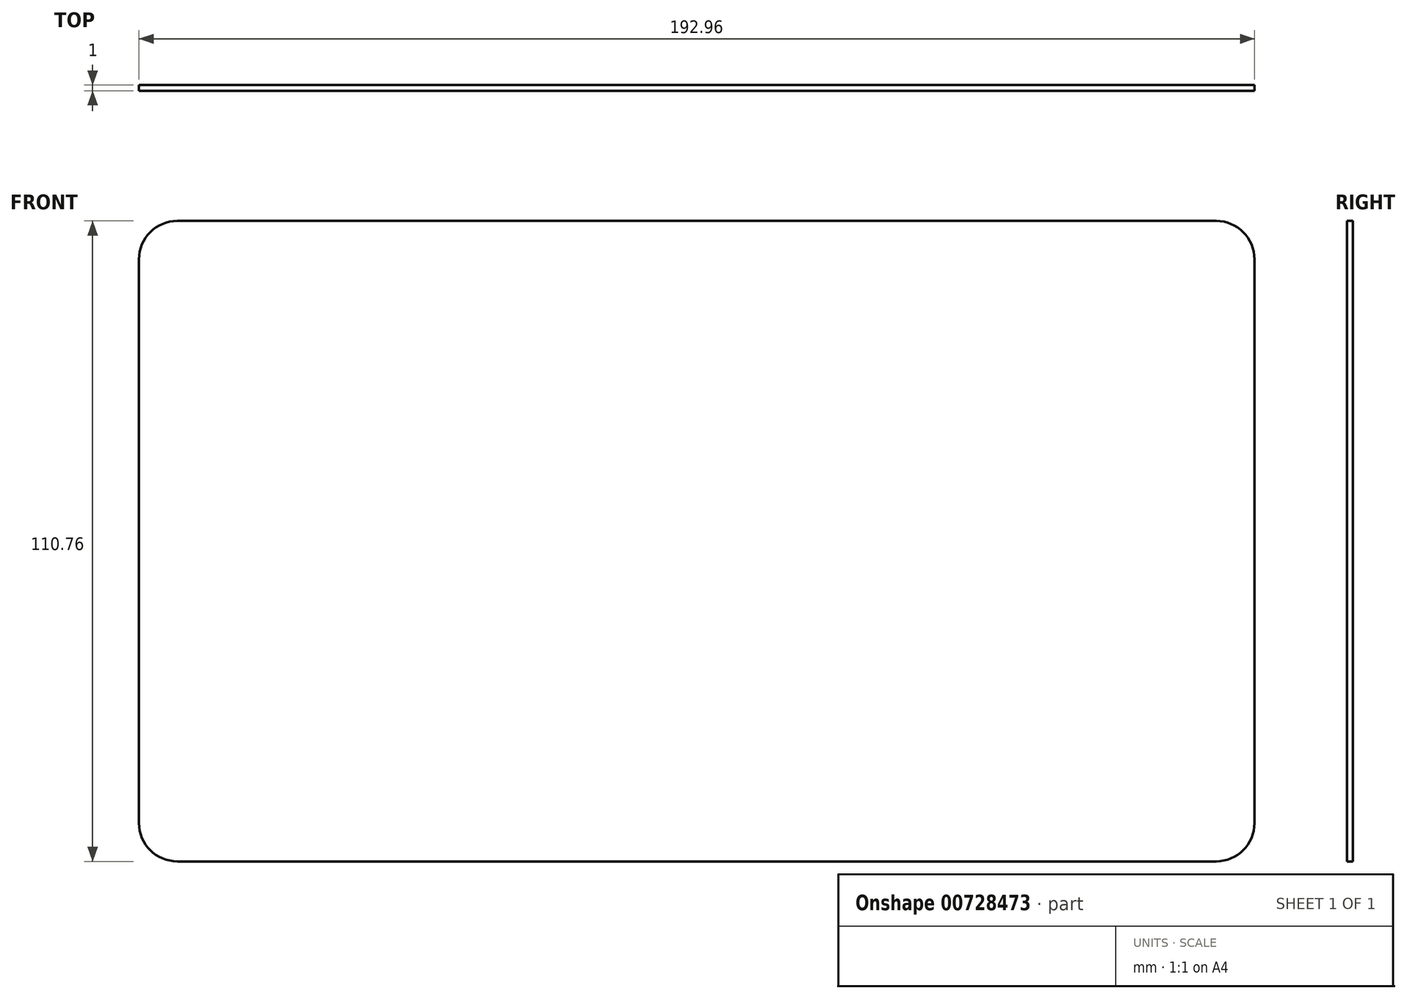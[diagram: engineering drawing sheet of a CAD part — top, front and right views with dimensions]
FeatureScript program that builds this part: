
annotation { "Feature Type Name" : "Feature", "Feature Type Description" : "" }
export const myFeature = defineFeature(function(context is Context, id is Id, definition is map)
    precondition{}
    {
        {
            var Q0;
            Q0=qCreatedBy(makeId("Front.planeOp"),FACE);
            var sketch = newSketch(context, id + "F0", { "sketchPlane" : qUnion([Q0])});
            skLineSegment(sketch, "E0.bottom", {"start": v(-89.85, 55.38) * mm, "end": v(89.85, 55.38) * mm});
            skLineSegment(sketch, "E0.top", {"start": v(-89.85, -55.38) * mm, "end": v(89.85, -55.38) * mm});
            skLineSegment(sketch, "E0.left", {"start": v(-96.48, 48.75) * mm, "end": v(-96.48, -48.75) * mm});
            skLineSegment(sketch, "E0.right", {"start": v(96.48, 48.75) * mm, "end": v(96.48, -48.75) * mm});
            skPoint(sketch, "E0.middle", {"position": v(0, 0) * mm});
            skPoint(sketch, "E1.visualSharp", {"position": v(-96.48, 55.38) * mm});
            skArc(sketch, "E1.filletArc", {"start": v(-89.85, 55.38) * mm, "mid": v(-94.54, 53.44) * mm, "end": v(-96.48, 48.75) * mm});
            skPoint(sketch, "E2.visualSharp", {"position": v(96.48, 55.38) * mm});
            skArc(sketch, "E2.filletArc", {"start": v(96.48, 48.75) * mm, "mid": v(94.54, 53.44) * mm, "end": v(89.85, 55.38) * mm});
            skPoint(sketch, "E3.visualSharp", {"position": v(96.48, -55.38) * mm});
            skArc(sketch, "E3.filletArc", {"start": v(89.85, -55.38) * mm, "mid": v(94.54, -53.44) * mm, "end": v(96.48, -48.75) * mm});
            skPoint(sketch, "E4.visualSharp", {"position": v(-96.48, -55.38) * mm});
            skArc(sketch, "E4.filletArc", {"start": v(-96.48, -48.75) * mm, "mid": v(-94.54, -53.44) * mm, "end": v(-89.85, -55.38) * mm});
            skLineSegment(sketch, "E5.bottom", {"start": v(-84.5, 48.75) * mm, "end": v(81.7, 48.75) * mm});
            skLineSegment(sketch, "E5.top", {"start": v(-84.5, -51.31) * mm, "end": v(81.7, -51.31) * mm});
            skLineSegment(sketch, "E5.left", {"start": v(-84.5, 48.75) * mm, "end": v(-84.5, -51.3) * mm});
            skLineSegment(sketch, "E5.right", {"start": v(81.7, 48.75) * mm, "end": v(81.7, -51.3) * mm});
            skPoint(sketch, "E5.middle", {"position": v(-1.4, -1.28) * mm});
            skLineSegment(sketch, "E6.bottom", {"start": v(-57.5, 29.8) * mm, "end": v(-71.5, 29.8) * mm});
            skLineSegment(sketch, "E6.top", {"start": v(-57.5, 37.8) * mm, "end": v(-71.5, 37.8) * mm});
            skLineSegment(sketch, "E6.left", {"start": v(-57.5, 29.8) * mm, "end": v(-57.5, 37.8) * mm});
            skLineSegment(sketch, "E6.right", {"start": v(-71.5, 29.8) * mm, "end": v(-71.5, 37.8) * mm});
            skPoint(sketch, "E6.middle", {"position": v(-64.5, 33.8) * mm});
            skLineSegment(sketch, "E7.bottom", {"start": v(68.7, 29.8) * mm, "end": v(54.7, 29.8) * mm});
            skLineSegment(sketch, "E7.top", {"start": v(68.7, 37.8) * mm, "end": v(54.7, 37.8) * mm});
            skLineSegment(sketch, "E7.left", {"start": v(68.7, 29.8) * mm, "end": v(68.7, 37.8) * mm});
            skLineSegment(sketch, "E7.right", {"start": v(54.7, 29.8) * mm, "end": v(54.7, 37.8) * mm});
            skPoint(sketch, "E7.middle", {"position": v(61.7, 33.8) * mm});
            skLineSegment(sketch, "E8.bottom", {"start": v(-57.5, -35.85) * mm, "end": v(-71.5, -35.85) * mm});
            skLineSegment(sketch, "E8.top", {"start": v(-57.5, -27.85) * mm, "end": v(-71.5, -27.85) * mm});
            skLineSegment(sketch, "E8.left", {"start": v(-57.5, -35.85) * mm, "end": v(-57.5, -27.85) * mm});
            skLineSegment(sketch, "E8.right", {"start": v(-71.5, -35.85) * mm, "end": v(-71.5, -27.85) * mm});
            skPoint(sketch, "E8.middle", {"position": v(-64.5, -31.85) * mm});
            skLineSegment(sketch, "E9.bottom", {"start": v(68.7, -35.85) * mm, "end": v(54.7, -35.85) * mm});
            skLineSegment(sketch, "E9.top", {"start": v(68.7, -27.85) * mm, "end": v(54.7, -27.85) * mm});
            skLineSegment(sketch, "E9.left", {"start": v(68.7, -35.85) * mm, "end": v(68.7, -27.85) * mm});
            skLineSegment(sketch, "E9.right", {"start": v(54.7, -35.85) * mm, "end": v(54.7, -27.85) * mm});
            skPoint(sketch, "E9.middle", {"position": v(61.7, -31.85) * mm});
            skCircle(sketch, "E10", {"center": v(-64.5, 33.8) * mm, "radius": 1.5 * mm});
            skCircle(sketch, "E11", {"center": v(61.7, 33.8) * mm, "radius": 1.5 * mm});
            skCircle(sketch, "E12", {"center": v(61.7, -31.85) * mm, "radius": 1.5 * mm});
            skCircle(sketch, "E13", {"center": v(-64.5, -31.85) * mm, "radius": 1.5 * mm});
            skLineSegment(sketch, "E14.bottom", {"start": v(-40.05, 20.95) * mm, "end": v(-32.05, 20.95) * mm});
            skLineSegment(sketch, "E14.top", {"start": v(-40.05, 34.95) * mm, "end": v(-32.05, 34.95) * mm});
            skLineSegment(sketch, "E14.left", {"start": v(-40.05, 20.95) * mm, "end": v(-40.05, 34.95) * mm});
            skLineSegment(sketch, "E14.right", {"start": v(-32.05, 20.95) * mm, "end": v(-32.05, 34.95) * mm});
            skPoint(sketch, "E14.middle", {"position": v(-36.05, 27.95) * mm});
            skLineSegment(sketch, "E15.bottom", {"start": v(-40.05, -14.05) * mm, "end": v(-32.05, -14.05) * mm});
            skLineSegment(sketch, "E15.top", {"start": v(-40.05, -28.05) * mm, "end": v(-32.05, -28.05) * mm});
            skLineSegment(sketch, "E15.left", {"start": v(-40.05, -14.05) * mm, "end": v(-40.05, -28.05) * mm});
            skLineSegment(sketch, "E15.right", {"start": v(-32.05, -14.05) * mm, "end": v(-32.05, -28.05) * mm});
            skPoint(sketch, "E15.middle", {"position": v(-36.05, -21.05) * mm});
            skLineSegment(sketch, "E16.bottom", {"start": v(17.95, -14.05) * mm, "end": v(25.95, -14.05) * mm});
            skLineSegment(sketch, "E16.top", {"start": v(17.95, -28.05) * mm, "end": v(25.95, -28.05) * mm});
            skLineSegment(sketch, "E16.left", {"start": v(17.95, -14.05) * mm, "end": v(17.95, -28.05) * mm});
            skLineSegment(sketch, "E16.right", {"start": v(25.95, -14.05) * mm, "end": v(25.95, -28.05) * mm});
            skPoint(sketch, "E16.middle", {"position": v(21.95, -21.05) * mm});
            skLineSegment(sketch, "E17.bottom", {"start": v(17.95, 20.95) * mm, "end": v(25.95, 20.95) * mm});
            skLineSegment(sketch, "E17.top", {"start": v(17.95, 34.95) * mm, "end": v(25.95, 34.95) * mm});
            skLineSegment(sketch, "E17.left", {"start": v(17.95, 20.95) * mm, "end": v(17.95, 34.95) * mm});
            skLineSegment(sketch, "E17.right", {"start": v(25.95, 20.95) * mm, "end": v(25.95, 34.95) * mm});
            skPoint(sketch, "E17.middle", {"position": v(21.95, 27.95) * mm});
            skCircle(sketch, "E18", {"center": v(-36.05, 27.95) * mm, "radius": 1.25 * mm});
            skCircle(sketch, "E19", {"center": v(21.95, 27.95) * mm, "radius": 1.25 * mm});
            skCircle(sketch, "E20", {"center": v(21.95, -21.05) * mm, "radius": 1.25 * mm});
            skCircle(sketch, "E21", {"center": v(-36.05, -21.05) * mm, "radius": 1.25 * mm});
            skLineSegment(sketch, "E22.bottom", {"start": v(-40.05, 24.95) * mm, "end": v(-32.05, 24.95) * mm});
            skLineSegment(sketch, "E22.top", {"start": v(-40.05, 30.95) * mm, "end": v(-32.05, 30.95) * mm});
            skLineSegment(sketch, "E22.left", {"start": v(-40.05, 24.95) * mm, "end": v(-40.05, 30.95) * mm});
            skLineSegment(sketch, "E22.right", {"start": v(-32.05, 24.95) * mm, "end": v(-32.05, 30.95) * mm});
            skLineSegment(sketch, "E23.bottom", {"start": v(17.95, 24.95) * mm, "end": v(25.95, 24.95) * mm});
            skLineSegment(sketch, "E23.top", {"start": v(17.95, 30.95) * mm, "end": v(25.95, 30.95) * mm});
            skLineSegment(sketch, "E23.left", {"start": v(17.95, 24.95) * mm, "end": v(17.95, 30.95) * mm});
            skLineSegment(sketch, "E23.right", {"start": v(25.95, 24.95) * mm, "end": v(25.95, 30.95) * mm});
            skLineSegment(sketch, "E24.bottom", {"start": v(17.95, -18.05) * mm, "end": v(25.95, -18.05) * mm});
            skLineSegment(sketch, "E24.top", {"start": v(17.95, -24.05) * mm, "end": v(25.95, -24.05) * mm});
            skLineSegment(sketch, "E24.left", {"start": v(17.95, -18.05) * mm, "end": v(17.95, -24.05) * mm});
            skLineSegment(sketch, "E24.right", {"start": v(25.95, -18.05) * mm, "end": v(25.95, -24.05) * mm});
            skLineSegment(sketch, "E25.bottom", {"start": v(-40.05, -18.05) * mm, "end": v(-32.05, -18.05) * mm});
            skLineSegment(sketch, "E25.top", {"start": v(-40.05, -24.05) * mm, "end": v(-32.05, -24.05) * mm});
            skLineSegment(sketch, "E25.left", {"start": v(-40.05, -18.05) * mm, "end": v(-40.05, -24.05) * mm});
            skLineSegment(sketch, "E25.right", {"start": v(-32.05, -18.05) * mm, "end": v(-32.05, -24.05) * mm});
            skLineSegment(sketch, "E26.bottom", {"start": v(-67.5, 37.8) * mm, "end": v(-61.5, 37.8) * mm});
            skLineSegment(sketch, "E26.top", {"start": v(-67.5, 29.8) * mm, "end": v(-61.5, 29.8) * mm});
            skLineSegment(sketch, "E26.left", {"start": v(-67.5, 37.8) * mm, "end": v(-67.5, 29.8) * mm});
            skLineSegment(sketch, "E26.right", {"start": v(-61.5, 37.8) * mm, "end": v(-61.5, 29.8) * mm});
            skLineSegment(sketch, "E27.bottom", {"start": v(-67.5, -27.85) * mm, "end": v(-61.5, -27.85) * mm});
            skLineSegment(sketch, "E27.top", {"start": v(-67.5, -35.85) * mm, "end": v(-61.5, -35.85) * mm});
            skLineSegment(sketch, "E27.left", {"start": v(-67.5, -27.85) * mm, "end": v(-67.5, -35.85) * mm});
            skLineSegment(sketch, "E27.right", {"start": v(-61.5, -27.85) * mm, "end": v(-61.5, -35.85) * mm});
            skLineSegment(sketch, "E28.bottom", {"start": v(58.7, -27.85) * mm, "end": v(64.7, -27.85) * mm});
            skLineSegment(sketch, "E28.top", {"start": v(58.7, -35.85) * mm, "end": v(64.7, -35.85) * mm});
            skLineSegment(sketch, "E28.left", {"start": v(58.7, -27.85) * mm, "end": v(58.7, -35.85) * mm});
            skLineSegment(sketch, "E28.right", {"start": v(64.7, -27.85) * mm, "end": v(64.7, -35.85) * mm});
            skLineSegment(sketch, "E29.bottom", {"start": v(58.7, 37.8) * mm, "end": v(64.7, 37.8) * mm});
            skLineSegment(sketch, "E29.top", {"start": v(58.7, 29.8) * mm, "end": v(64.7, 29.8) * mm});
            skLineSegment(sketch, "E29.left", {"start": v(58.7, 37.8) * mm, "end": v(58.7, 29.8) * mm});
            skLineSegment(sketch, "E29.right", {"start": v(64.7, 37.8) * mm, "end": v(64.7, 29.8) * mm});
            skSolve(sketch);
        }
        {
            var Q0;
            Q0=makeQuery(id+"F0.imprint","IMPRINT",FACE,{"disambiguationData":[TD([[makeQuery(id+"F0.imprint","IMPRINT",EDGE,{"derivedFrom":sQuery(id+"F0.wireOp",EDGE,"E13")}),-1.0]])]});
            var Q1;
            {var subQ0=sQuery(id+"F0.wireOp",EDGE,"E17.top");Q1=makeQuery(id+"F0.imprint","IMPRINT",FACE,{"disambiguationData":[TD([[makeQuery(id+"F0.imprint","IMPRINT",EDGE,{"derivedFrom":subQ0}),-1.0]])]});}
            var Q2;
            Q2=makeQuery(id+"F0.imprint","IMPRINT",FACE,{"disambiguationData":[TD([[makeQuery(id+"F0.imprint","IMPRINT",EDGE,{"derivedFrom":sQuery(id+"F0.wireOp",EDGE,"E5.bottom")}),-1.0]])]});
            var Q3;
            {var subQ0=sQuery(id+"F0.wireOp",EDGE,"E14.bottom");Q3=makeQuery(id+"F0.imprint","IMPRINT",FACE,{"disambiguationData":[TD([[makeQuery(id+"F0.imprint","IMPRINT",EDGE,{"derivedFrom":subQ0}),1.0]])]});}
            var Q4;
            Q4=makeQuery(id+"F0.imprint","IMPRINT",FACE,{"disambiguationData":[TD([[makeQuery(id+"F0.imprint","IMPRINT",EDGE,{"derivedFrom":sQuery(id+"F0.wireOp",EDGE,"E19")}),-1.0]])]});
            var Q5;
            {var subQ0=sQuery(id+"F0.wireOp",EDGE,"E16.bottom");Q5=makeQuery(id+"F0.imprint","IMPRINT",FACE,{"disambiguationData":[TD([[makeQuery(id+"F0.imprint","IMPRINT",EDGE,{"derivedFrom":subQ0}),-1.0]])]});}
            var Q6;
            {var subQ0=sQuery(id+"F0.wireOp",EDGE,"E17.bottom");Q6=makeQuery(id+"F0.imprint","IMPRINT",FACE,{"disambiguationData":[TD([[makeQuery(id+"F0.imprint","IMPRINT",EDGE,{"derivedFrom":subQ0}),1.0]])]});}
            var Q7;
            Q7=makeQuery(id+"F0.imprint","IMPRINT",FACE,{"disambiguationData":[TD([[makeQuery(id+"F0.imprint","IMPRINT",EDGE,{"derivedFrom":sQuery(id+"F0.wireOp",EDGE,"E12")}),-1.0]])]});
            var Q8;
            Q8=makeQuery(id+"F0.imprint","IMPRINT",FACE,{"disambiguationData":[TD([[makeQuery(id+"F0.imprint","IMPRINT",EDGE,{"derivedFrom":sQuery(id+"F0.wireOp",EDGE,"E21")}),-1.0]])]});
            var Q9;
            {var subQ0=sQuery(id+"F0.wireOp",EDGE,"E7.right");Q9=makeQuery(id+"F0.imprint","IMPRINT",FACE,{"disambiguationData":[TD([[makeQuery(id+"F0.imprint","IMPRINT",EDGE,{"derivedFrom":subQ0}),-1.0]])]});}
            var Q10;
            {var subQ0=sQuery(id+"F0.wireOp",EDGE,"E7.left");Q10=makeQuery(id+"F0.imprint","IMPRINT",FACE,{"disambiguationData":[TD([[makeQuery(id+"F0.imprint","IMPRINT",EDGE,{"derivedFrom":subQ0}),1.0]])]});}
            var Q11;
            {var subQ0=sQuery(id+"F0.wireOp",EDGE,"E6.right");Q11=makeQuery(id+"F0.imprint","IMPRINT",FACE,{"disambiguationData":[TD([[makeQuery(id+"F0.imprint","IMPRINT",EDGE,{"derivedFrom":subQ0}),-1.0]])]});}
            var Q12;
            {var subQ0=sQuery(id+"F0.wireOp",EDGE,"E6.left");Q12=makeQuery(id+"F0.imprint","IMPRINT",FACE,{"disambiguationData":[TD([[makeQuery(id+"F0.imprint","IMPRINT",EDGE,{"derivedFrom":subQ0}),1.0]])]});}
            var Q13;
            {var subQ0=sQuery(id+"F0.wireOp",EDGE,"E9.right");Q13=makeQuery(id+"F0.imprint","IMPRINT",FACE,{"disambiguationData":[TD([[makeQuery(id+"F0.imprint","IMPRINT",EDGE,{"derivedFrom":subQ0}),-1.0]])]});}
            var Q14;
            {var subQ0=sQuery(id+"F0.wireOp",EDGE,"E8.left");Q14=makeQuery(id+"F0.imprint","IMPRINT",FACE,{"disambiguationData":[TD([[makeQuery(id+"F0.imprint","IMPRINT",EDGE,{"derivedFrom":subQ0}),1.0]])]});}
            var Q15;
            Q15=makeQuery(id+"F0.imprint","IMPRINT",FACE,{"disambiguationData":[TD([[makeQuery(id+"F0.imprint","IMPRINT",EDGE,{"derivedFrom":sQuery(id+"F0.wireOp",EDGE,"E0.bottom")}),-1.0]])]});
            var Q16;
            {var subQ0=sQuery(id+"F0.wireOp",EDGE,"E8.right");Q16=makeQuery(id+"F0.imprint","IMPRINT",FACE,{"disambiguationData":[TD([[makeQuery(id+"F0.imprint","IMPRINT",EDGE,{"derivedFrom":subQ0}),-1.0]])]});}
            var Q17;
            {var subQ0=sQuery(id+"F0.wireOp",EDGE,"E15.top");Q17=makeQuery(id+"F0.imprint","IMPRINT",FACE,{"disambiguationData":[TD([[makeQuery(id+"F0.imprint","IMPRINT",EDGE,{"derivedFrom":subQ0}),1.0]])]});}
            var Q18;
            {var subQ0=sQuery(id+"F0.wireOp",EDGE,"E16.top");Q18=makeQuery(id+"F0.imprint","IMPRINT",FACE,{"disambiguationData":[TD([[makeQuery(id+"F0.imprint","IMPRINT",EDGE,{"derivedFrom":subQ0}),1.0]])]});}
            var Q19;
            {var subQ0=sQuery(id+"F0.wireOp",EDGE,"E9.left");Q19=makeQuery(id+"F0.imprint","IMPRINT",FACE,{"disambiguationData":[TD([[makeQuery(id+"F0.imprint","IMPRINT",EDGE,{"derivedFrom":subQ0}),1.0]])]});}
            var Q20;
            Q20=makeQuery(id+"F0.imprint","IMPRINT",FACE,{"disambiguationData":[TD([[makeQuery(id+"F0.imprint","IMPRINT",EDGE,{"derivedFrom":sQuery(id+"F0.wireOp",EDGE,"E18")}),-1.0]])]});
            var Q21;
            {var subQ0=sQuery(id+"F0.wireOp",EDGE,"E15.bottom");Q21=makeQuery(id+"F0.imprint","IMPRINT",FACE,{"disambiguationData":[TD([[makeQuery(id+"F0.imprint","IMPRINT",EDGE,{"derivedFrom":subQ0}),-1.0]])]});}
            var Q22;
            Q22=makeQuery(id+"F0.imprint","IMPRINT",FACE,{"disambiguationData":[TD([[makeQuery(id+"F0.imprint","IMPRINT",EDGE,{"derivedFrom":sQuery(id+"F0.wireOp",EDGE,"E11")}),-1.0]])]});
            var Q23;
            {var subQ0=sQuery(id+"F0.wireOp",EDGE,"E14.top");Q23=makeQuery(id+"F0.imprint","IMPRINT",FACE,{"disambiguationData":[TD([[makeQuery(id+"F0.imprint","IMPRINT",EDGE,{"derivedFrom":subQ0}),-1.0]])]});}
            var Q24;
            Q24=makeQuery(id+"F0.imprint","IMPRINT",FACE,{"disambiguationData":[TD([[makeQuery(id+"F0.imprint","IMPRINT",EDGE,{"derivedFrom":sQuery(id+"F0.wireOp",EDGE,"E20")}),-1.0]])]});
            var Q25;
            Q25=makeQuery(id+"F0.imprint","IMPRINT",FACE,{"disambiguationData":[TD([[makeQuery(id+"F0.imprint","IMPRINT",EDGE,{"derivedFrom":sQuery(id+"F0.wireOp",EDGE,"E10")}),-1.0]])]});
            var Q26;
            Q26=makeQuery(id+"F0.imprint","IMPRINT",FACE,{"disambiguationData":[TD([[makeQuery(id+"F0.imprint","IMPRINT",EDGE,{"derivedFrom":sQuery(id+"F0.wireOp",EDGE,"E10")}),1.0]])]});
            var Q27;
            Q27=makeQuery(id+"F0.imprint","IMPRINT",FACE,{"disambiguationData":[TD([[makeQuery(id+"F0.imprint","IMPRINT",EDGE,{"derivedFrom":sQuery(id+"F0.wireOp",EDGE,"E11")}),1.0]])]});
            var Q28;
            Q28=makeQuery(id+"F0.imprint","IMPRINT",FACE,{"disambiguationData":[TD([[makeQuery(id+"F0.imprint","IMPRINT",EDGE,{"derivedFrom":sQuery(id+"F0.wireOp",EDGE,"E21")}),1.0]])]});
            var Q29;
            Q29=makeQuery(id+"F0.imprint","IMPRINT",FACE,{"disambiguationData":[TD([[makeQuery(id+"F0.imprint","IMPRINT",EDGE,{"derivedFrom":sQuery(id+"F0.wireOp",EDGE,"E20")}),1.0]])]});
            var Q30;
            Q30=makeQuery(id+"F0.imprint","IMPRINT",FACE,{"disambiguationData":[TD([[makeQuery(id+"F0.imprint","IMPRINT",EDGE,{"derivedFrom":sQuery(id+"F0.wireOp",EDGE,"E19")}),1.0]])]});
            var Q31;
            Q31=makeQuery(id+"F0.imprint","IMPRINT",FACE,{"disambiguationData":[TD([[makeQuery(id+"F0.imprint","IMPRINT",EDGE,{"derivedFrom":sQuery(id+"F0.wireOp",EDGE,"E18")}),1.0]])]});
            var Q32;
            Q32=makeQuery(id+"F0.imprint","IMPRINT",FACE,{"disambiguationData":[TD([[makeQuery(id+"F0.imprint","IMPRINT",EDGE,{"derivedFrom":sQuery(id+"F0.wireOp",EDGE,"E13")}),1.0]])]});
            var Q33;
            Q33=makeQuery(id+"F0.imprint","IMPRINT",FACE,{"disambiguationData":[TD([[makeQuery(id+"F0.imprint","IMPRINT",EDGE,{"derivedFrom":sQuery(id+"F0.wireOp",EDGE,"E12")}),1.0]])]});
            extrude(context, id + "F1", {"entities" : qUnion([Q0, Q1, Q2, Q3, Q4, Q5, Q6, Q7, Q8, Q9, Q10, Q11, Q12, Q13, Q14, Q15, Q16, Q17, Q18, Q19, Q20, Q21, Q22, Q23, Q24, Q25, Q26, Q27, Q28, Q29, Q30, Q31, Q32, Q33]), "oppositeDirection" : true, "depth" : 1 * mm, "offsetDistance" : 25 * mm});
        }
    });
